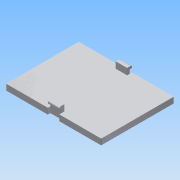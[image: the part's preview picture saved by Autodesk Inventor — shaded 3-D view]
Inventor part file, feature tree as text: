
AUTODESK INVENTOR PART (.ipt)
format: ipt  version: 2015 SP1 (Build 190203100, 203)  size: 188,416 bytes
history: native  units: mm
features: extrude x4, sketch x4, fillet x2, other x1
ambient origin geometry x8: Origin, YZ Plane, XZ Plane, XY Plane, X Axis, Y Axis, Z Axis, Center Point
bodies: Body1 (feature_tree)
feature tree (11):
  other  "Твердое тело1"
  extrude  "Выдавливание1"  Depth=42.0mm
  extrude  "Выдавливание3"  Depth=32.1mm
  extrude  "Выдавливание4"  Depth=2.7mm TaperAngle=0.0deg
  extrude  "Выдавливание5"  Depth=5.0mm
  fillet  "Сопряжение1"  Radius=1.0mm
  fillet  "Сопряжение2"  Radius=5.0mm
  sketch  "Эскиз1"
  sketch  "Эскиз3"
  sketch  "Эскиз4"
  sketch  "Эскиз5"
